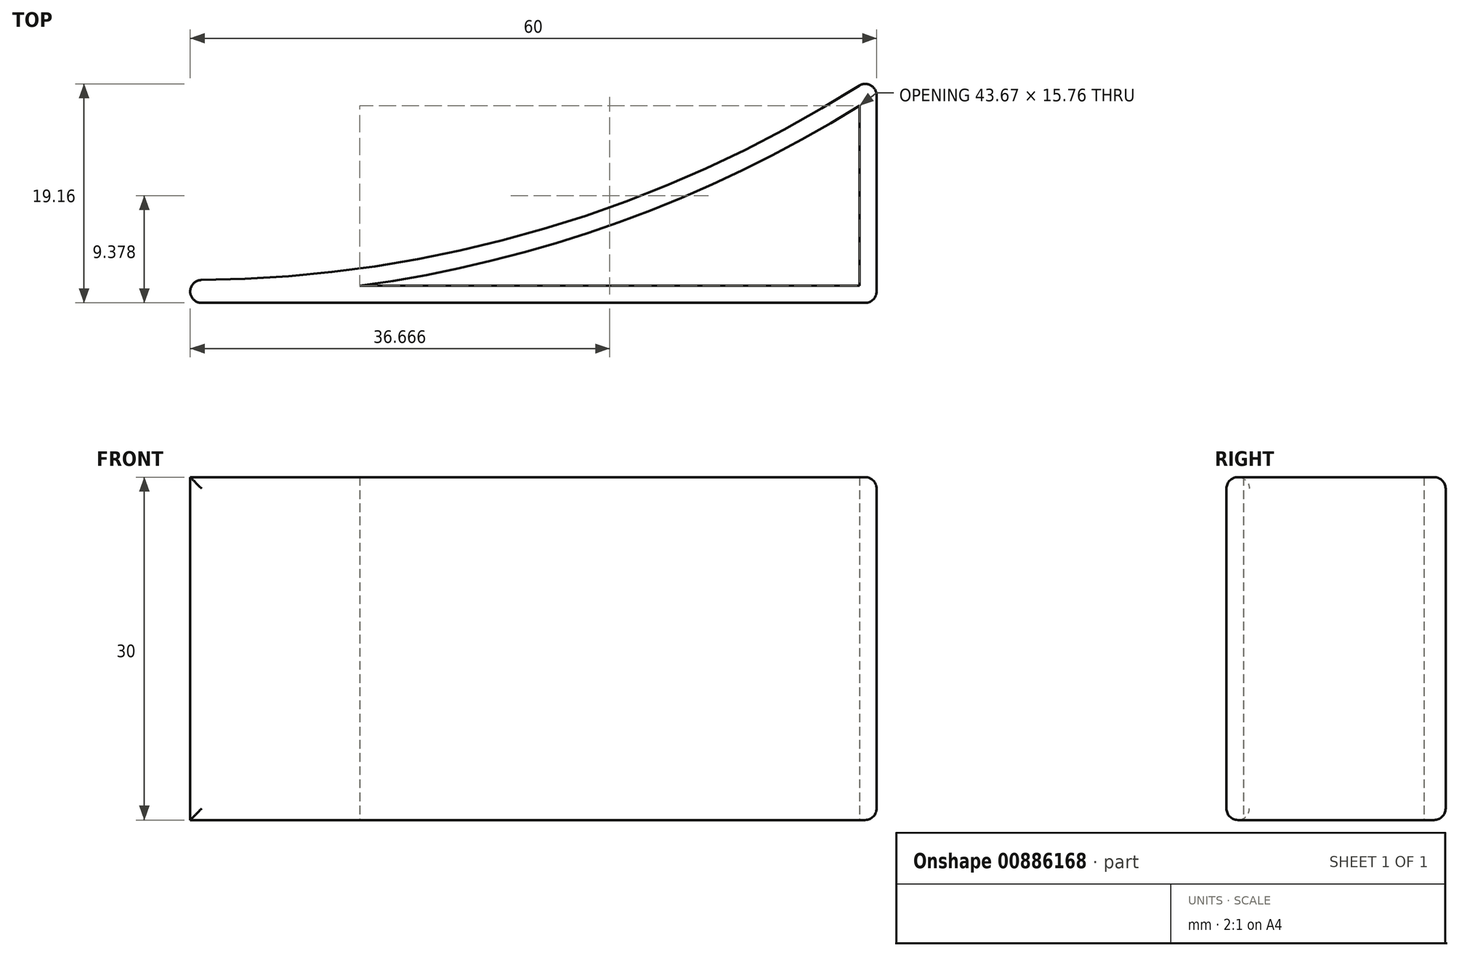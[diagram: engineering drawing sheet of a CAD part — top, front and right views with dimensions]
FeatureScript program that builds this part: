
annotation { "Feature Type Name" : "Feature", "Feature Type Description" : "" }
export const myFeature = defineFeature(function(context is Context, id is Id, definition is map)
    precondition{}
    {
        {
            var Q0;
            Q0=qCreatedBy(makeId("Top.planeOp"),FACE);
            var sketch = newSketch(context, id + "F0", { "sketchPlane" : qUnion([Q0])});
            skLineSegment(sketch, "E0", {"start": v(-60, 0) * mm, "end": v(0, 0) * mm});
            skLineSegment(sketch, "E1", {"start": v(0, 0) * mm, "end": v(0, 20) * mm});
            skLineSegment(sketch, "E2", {"start": v(-60, 0) * mm, "end": v(-60, 2) * mm});
            skArc(sketch, "E3", {"start": v(-60, 2) * mm, "mid": v(-28.68, 6.6) * mm, "end": v(0, 20) * mm});
            skSolve(sketch);
        }
        {
            var Q0;
            Q0=makeQuery(id+"F0.imprint","IMPRINT",FACE,{"disambiguationData":[TD([[makeQuery(id+"F0.imprint","IMPRINT",EDGE,{"derivedFrom":sQuery(id+"F0.wireOp",EDGE,"E0")}),1.0]])]});
            extrude(context, id + "F1", {"entities" : qUnion([Q0]), "depth" : 30 * mm, "offsetDistance" : 25 * mm});
        }
        {
            var Q0;
            Q0=makeQuery(id+"F1.opExtrude","CAP_FACE",FACE,{"disambiguationData":[OSD([sQuery(id+"F0.wireOp",EDGE,"E0"),sQuery(id+"F0.wireOp",EDGE,"E1"),sQuery(id+"F0.wireOp",EDGE,"E2"),sQuery(id+"F0.wireOp",EDGE,"E3")])],"isStart":false});
            var Q1;
            Q1=makeQuery(id+"F1.opExtrude","CAP_FACE",FACE,{"disambiguationData":[OSD([sQuery(id+"F0.wireOp",EDGE,"E0"),sQuery(id+"F0.wireOp",EDGE,"E1"),sQuery(id+"F0.wireOp",EDGE,"E2"),sQuery(id+"F0.wireOp",EDGE,"E3")])],"isStart":true});
            shell(context, id + "F2", {"entities" : qUnion([Q0, Q1]), "thickness" : 1.5 * mm});
        }
        {
            var Q0;
            Q0=makeQuery(id+"F1.opExtrude","SWEPT_EDGE",EDGE,{"disambiguationData":[OSD([sQuery(id+"F0.wireOp",EDGE,"E2"),sQuery(id+"F0.wireOp",EDGE,"E3")])]});
            var Q1;
            Q1=makeQuery(id+"F1.opExtrude","SWEPT_EDGE",EDGE,{"disambiguationData":[OSD([sQuery(id+"F0.wireOp",EDGE,"E0"),sQuery(id+"F0.wireOp",EDGE,"E2")])]});
            var Q2;
            Q2=makeQuery(id+"F1.opExtrude","CAP_EDGE",EDGE,{"disambiguationData":[OSD([sQuery(id+"F0.wireOp",EDGE,"E3")])],"isStart":false});
            var Q3;
            Q3=makeQuery(id+"F1.opExtrude","CAP_EDGE",EDGE,{"disambiguationData":[OSD([sQuery(id+"F0.wireOp",EDGE,"E0")])],"isStart":false});
            var Q4;
            Q4=makeQuery(id+"F1.opExtrude","CAP_EDGE",EDGE,{"disambiguationData":[OSD([sQuery(id+"F0.wireOp",EDGE,"E3")])],"isStart":true});
            var Q5;
            Q5=makeQuery(id+"F1.opExtrude","CAP_EDGE",EDGE,{"disambiguationData":[OSD([sQuery(id+"F0.wireOp",EDGE,"E0")])],"isStart":true});
            var Q6;
            Q6=makeQuery(id+"F1.opExtrude","SWEPT_EDGE",EDGE,{"disambiguationData":[OSD([sQuery(id+"F0.wireOp",EDGE,"E1"),sQuery(id+"F0.wireOp",EDGE,"E3")])]});
            var Q7;
            Q7=makeQuery(id+"F1.opExtrude","SWEPT_EDGE",EDGE,{"disambiguationData":[OSD([sQuery(id+"F0.wireOp",EDGE,"E0"),sQuery(id+"F0.wireOp",EDGE,"E1")])]});
            var Q8;
            Q8=makeQuery(id+"F1.opExtrude","CAP_EDGE",EDGE,{"disambiguationData":[OSD([sQuery(id+"F0.wireOp",EDGE,"E1")])],"isStart":false});
            var Q9;
            Q9=makeQuery(id+"F1.opExtrude","CAP_EDGE",EDGE,{"disambiguationData":[OSD([sQuery(id+"F0.wireOp",EDGE,"E1")])],"isStart":true});
            fillet(context, id + "F3", {"entities" : qUnion([Q0, Q1, Q2, Q3, Q4, Q5, Q6, Q7, Q8, Q9]), "radius" : 1 * mm, "tangentPropagation" : true, "allowEdgeOverflow" : false});
        }
    });
